# Revit family: Floors_Floor-Construction-Pedestal_Buzon_PB-5_inserts
name_source: partatom
category: Generic Models
revit_build: Autodesk Revit 2015 (Build: 20140606_1530(x64)
units: mm (PartAtom-declared; Revit-internal decimal feet)

## types (1)
- PB 5
    Brand url = http://www.buzon-world.com
    Default Elevation = 1219 mm
    Design country = Belgium
    Edition number = 1
    Manufacturer country = Belgium
    Manufacturer name = Buzon
    Material main = Polypropylene
    Material secondary = Polypropylene
    Nominal height = 0 mm  [stored 0 ft]
    Nominal width = 0 mm  [stored 0 ft]
    Product Guid = 16be64be-0cc7-4117-a733-38b709011bb6
    Product Material = Default_PB_Material
    Product SKU = PB-5
    Product data url = https://bimobject.com
    Product family = PB
    Product group = Pedestal
    Product url = http://www.buzon-world.com
    QR code = http://bimobject.com

note: [stored X ft] marks values corroborated as IEEE doubles in the binary element streams (Revit-internal decimal feet)

## geometry (parser evidence)
native form markers: Sweep x23
no freeform markers — native parametric forms only
